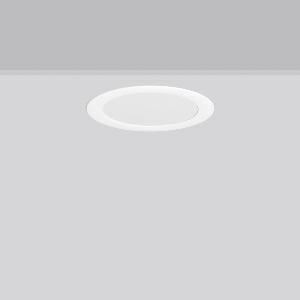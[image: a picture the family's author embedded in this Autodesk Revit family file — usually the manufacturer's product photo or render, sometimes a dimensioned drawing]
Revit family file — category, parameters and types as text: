
# Revit family: toledo_flat_round_e_672230_002_1_3b37
name_source: partatom
category: Lighting Fixtures
units: mm (PartAtom-declared; Revit-internal decimal feet)

## family parameters
Cut with Voids When Loaded = No
Host = Face
Light Source = No
Part Type = Normal
Room Calculation Point = No
Round Connector Dimension = Use Diameter
Shared = No

## types (1)
- TOLEDO FLAT round E (1 x LED Modul 840, 1800 lm, 4000)
    Apparent Load = 17 VA
    CIE Flux Codes = 48 79 96 100 100
    Color Rendering = 80
    Color Temperature = 4000
    Default Elevation = 1800 mm  [stored 5.90551 ft]
    Description = Series: TOLEDO FLAT round
Ultra thin recessed downlight. For escape route illumination. Housing: die-cast aluminium, powder-coated. Lightguide and diffuser made of non-yellowing plastic (PMMA). Diffuser opal matt plastic. Ceiling installation with spring system. Including separate LED converter with connecting cable 250 mm. Suitable for connection to central battery systems. External driver with simple plug-in locking system. 
Colour: white
Diameter: 255 mm
Height: 3 mm
Cut-out diameter: 234 mm
Recess height: 35 mm
Luminaire: recess height: 31-51 mm
Weight: 0.81 kg
Operating mode: maintained power mode
Lamp: LED
Socket: without socket
Colour temperature: 4000K
Colour rendering index (CRI): 80
System power: 17 W
Rated luminous flux: 1800 lm
Luminous flux, emergency: 1800 lm
System power, emergency: 17 W
Control gear: Regulated power supply
Protection class: II
Type of protection: IP 54
    Height = 0 mm  [stored 0 ft]
    Lamp = 1 x LED Modul 840
    Lamp Light Flux = 1800 lm
    Lamp count = 1
    Length = 255 mm
    Lifetime = 50000 h
    Luminous efficacy = 106 lm/W
    Manufacturer = RZB
    ModVariant = No
    Model = 672230.002.1
    Mounting Place = Ceiling
    Mounting Type = Recessed
    Number of Poles = 1
    OnlyDefault = Yes
    Power Factor = 1
    Product Name = TOLEDO FLAT round E
    Product group = Recessed downlights
    ProductGroupID = 402
    Protection Class = Protection class II
    Protection Degree = IP 40
    RLX_Detail_Level = 1
    RLX_Emergency_Light_Flux = 1800 lm
    RLX_Emergency_Type = 3
    RLX_Emergency_Type_DB = Yes
    RlxData = <blob elided: 30301 chars, md5=5b57e7bd>
    Socket = socket
    Standby Power = 0 W
    System Light Flux = 1800 lm
    System Power = 17 W
    Type Comments = Product without accessories
    Type Image = 901453.002.jpg
    URL = http://relux.com
    VarID = ---
    Voltage = 230 V
    Voltage Range = 220-240 V
    Weight = 0.00 kg
    Width = 0 mm  [stored 0 ft]

note: [stored X ft] marks values corroborated as IEEE doubles in the binary element streams (Revit-internal decimal feet)

## geometry (parser evidence)
native form markers: Blend x4, Sweep x11
no freeform markers — native parametric forms only
